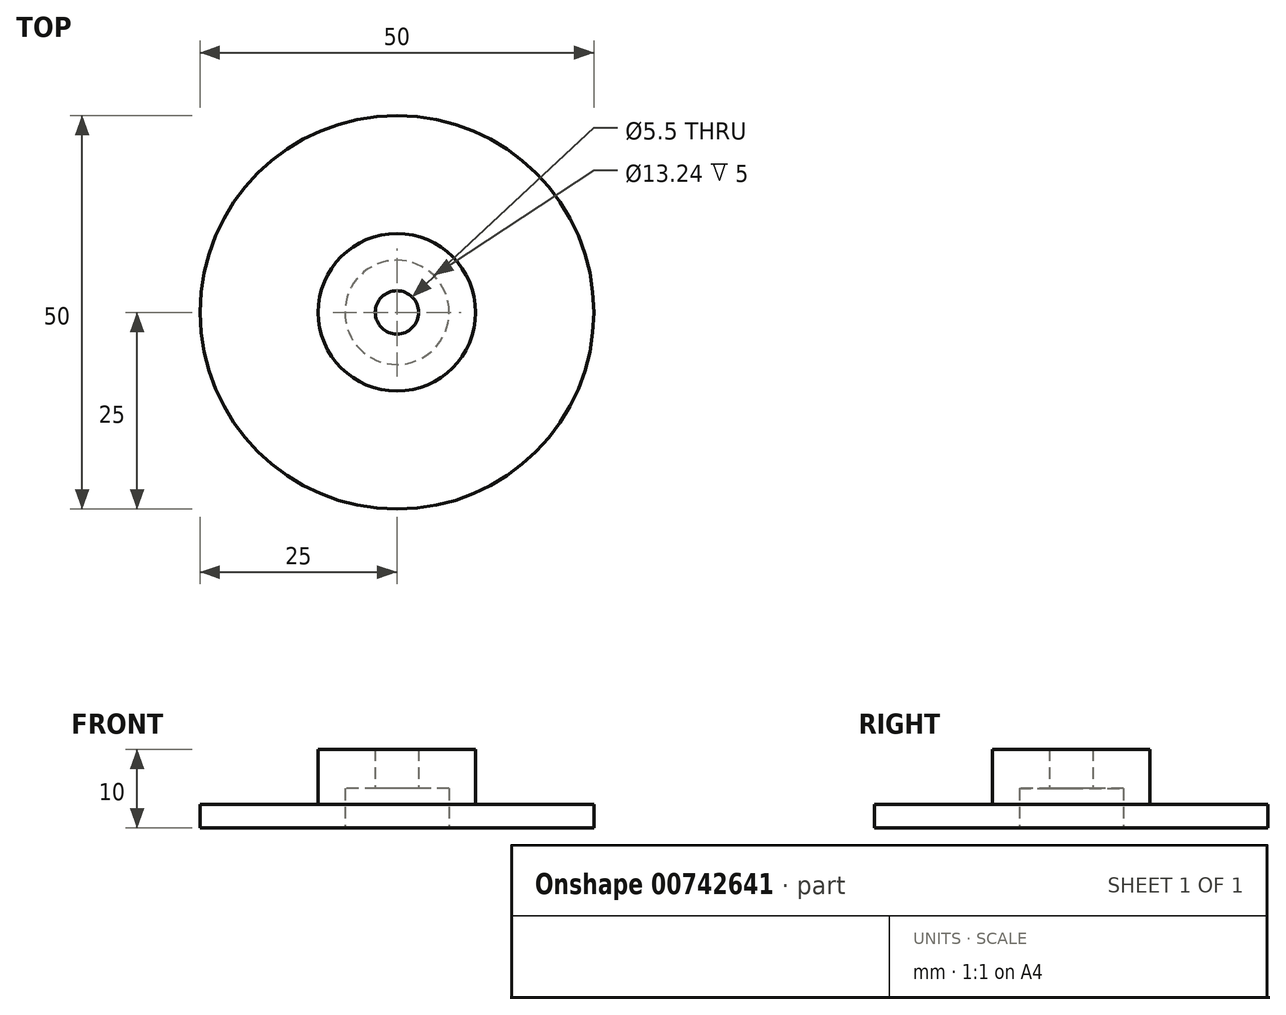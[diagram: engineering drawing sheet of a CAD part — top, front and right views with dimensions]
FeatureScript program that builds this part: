
annotation { "Feature Type Name" : "Feature", "Feature Type Description" : "" }
export const myFeature = defineFeature(function(context is Context, id is Id, definition is map)
    precondition{}
    {
        {
            var Q0;
            Q0=qCreatedBy(makeId("Top.planeOp"),FACE);
            var sketch = newSketch(context, id + "F0", { "sketchPlane" : qUnion([Q0])});
            skCircle(sketch, "E0", {"center": v(0, 0) * mm, "radius": 25 * mm});
            skCircle(sketch, "E1", {"center": v(0, 0) * mm, "radius": 10 * mm});
            skSolve(sketch);
        }
        {
            var Q0;
            Q0=makeQuery(id+"F0.imprint","IMPRINT",FACE,{"disambiguationData":[TD([[makeQuery(id+"F0.imprint","IMPRINT",EDGE,{"derivedFrom":sQuery(id+"F0.wireOp",EDGE,"E0")}),1.0]])]});
            var Q1;
            Q1=makeQuery(id+"F0.imprint","IMPRINT",FACE,{"disambiguationData":[TD([[makeQuery(id+"F0.imprint","IMPRINT",EDGE,{"derivedFrom":sQuery(id+"F0.wireOp",EDGE,"E1")}),1.0]])]});
            extrude(context, id + "F1", {"entities" : qUnion([Q0, Q1]), "depth" : 3 * mm, "offsetDistance" : 25 * mm});
        }
        {
            var Q0;
            Q0=makeQuery(id+"F0.imprint","IMPRINT",FACE,{"disambiguationData":[TD([[makeQuery(id+"F0.imprint","IMPRINT",EDGE,{"derivedFrom":sQuery(id+"F0.wireOp",EDGE,"E1")}),1.0]])]});
            extrude(context, id + "F2", {"entities" : qUnion([Q0]), "operationType" : NewBodyOperationType.ADD, "depth" : 10 * mm, "offsetDistance" : 25 * mm});
        }
        {
            var Q0;
            Q0=sQuery(id+"F0.wireOp",VERTEX,"E0.center");
            var Q1;
            Q1=makeQuery(id+"F1.opExtrude","SWEPT_BODY",BODY,{"disambiguationData":[OSD([sQuery(id+"F0.wireOp",EDGE,"E0")])]});
            hole(context, id + "F3", {"style" : HoleStyle.SIMPLE, "endStyle" : HoleEndStyle.BLIND, "oppositeDirection" : true, "holeDiameter" : 5.5 * mm, "majorDiameter" : 5 * mm, "holeDepth" : 30 * mm, "isTappedThrough" : true, "tappedDepth" : 10.5 * mm, "tapClearance" : 3, "locations" : qUnion([Q0]), "scope" : qUnion([Q1])});
        }
        {
            var Q0;
            Q0=makeQuery(id+"F0.imprint","IMPRINT",FACE,{"disambiguationData":[TD([[makeQuery(id+"F0.imprint","IMPRINT",EDGE,{"derivedFrom":sQuery(id+"F0.wireOp",EDGE,"E1")}),1.0]])]});
            var sketch = newSketch(context, id + "F4", { "sketchPlane" : qUnion([Q0])});
            skCircle(sketch, "E2.cCircle", {"center": v(0, 0) * mm, "radius": 4.2 * mm, "construction": true});
            skLineSegment(sketch, "E2.0", {"start": v(-2.42, 4.2) * mm, "end": v(2.42, 4.2) * mm});
            skLineSegment(sketch, "E2.1", {"start": v(2.42, 4.2) * mm, "end": v(4.85, 0) * mm});
            skLineSegment(sketch, "E2.2", {"start": v(4.85, 0) * mm, "end": v(2.42, -4.2) * mm});
            skLineSegment(sketch, "E2.3", {"start": v(2.42, -4.2) * mm, "end": v(-2.42, -4.2) * mm});
            skLineSegment(sketch, "E2.4", {"start": v(-2.42, -4.2) * mm, "end": v(-4.85, 0) * mm});
            skLineSegment(sketch, "E2.5", {"start": v(-4.85, 0) * mm, "end": v(-2.42, 4.2) * mm});
            skPoint(sketch, "E2.0.midPoint", {"position": v(0, 4.2) * mm});
            skCircle(sketch, "E3", {"center": v(0, 0) * mm, "radius": 6.62 * mm});
            skSolve(sketch);
        }
        {
            var Q0;
            Q0=makeQuery(id+"F4.imprint","IMPRINT",FACE,{"disambiguationData":[TD([[makeQuery(id+"F4.imprint","IMPRINT",EDGE,{"derivedFrom":sQuery(id+"F4.wireOp",EDGE,"E2.0")}),-1.0]])]});
            var Q1;
            Q1=makeQuery(id+"F4.imprint","IMPRINT",FACE,{"disambiguationData":[TD([[makeQuery(id+"F4.imprint","IMPRINT",EDGE,{"derivedFrom":sQuery(id+"F4.wireOp",EDGE,"E2.0")}),1.0]])]});
            extrude(context, id + "F5", {"entities" : qUnion([Q0, Q1]), "operationType" : NewBodyOperationType.REMOVE, "depth" : 5 * mm, "offsetDistance" : 25 * mm});
        }
    });
